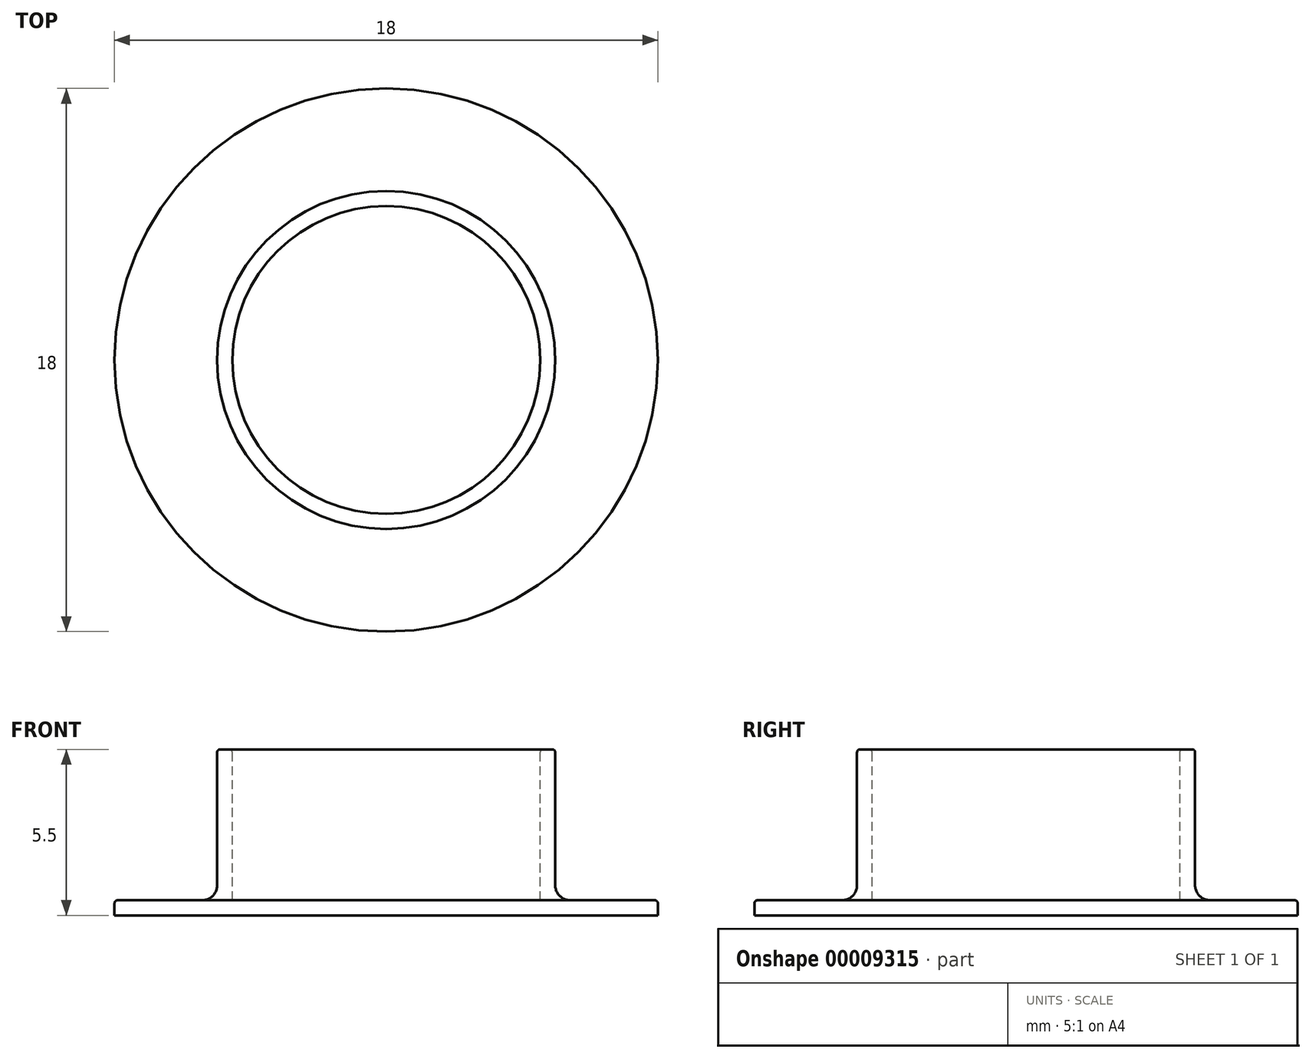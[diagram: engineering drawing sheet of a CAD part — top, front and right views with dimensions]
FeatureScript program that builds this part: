
annotation { "Feature Type Name" : "Feature", "Feature Type Description" : "" }
export const myFeature = defineFeature(function(context is Context, id is Id, definition is map)
    precondition{}
    {
        {
            var Q0;
            Q0=qCreatedBy(makeId("Right.planeOp"),FACE);
            var sketch = newSketch(context, id + "F0", { "sketchPlane" : qUnion([Q0])});
            skLineSegment(sketch, "E0", {"start": v(0, 0) * mm, "end": v(-9, 0) * mm});
            skLineSegment(sketch, "E1", {"start": v(-9, 0) * mm, "end": v(-9, 0.4) * mm});
            skLineSegment(sketch, "E2", {"start": v(-8.9, 0.5) * mm, "end": v(-6.1, 0.5) * mm});
            skLineSegment(sketch, "E3", {"start": v(0, 0.5) * mm, "end": v(0, 0) * mm});
            skLineSegment(sketch, "E4", {"start": v(-5.1, 0.5) * mm, "end": v(-5.1, 5.4) * mm});
            skLineSegment(sketch, "E5", {"start": v(-5.2, 5.5) * mm, "end": v(-5.5, 5.5) * mm});
            skLineSegment(sketch, "E6", {"start": v(-5.6, 5.4) * mm, "end": v(-5.6, 1) * mm});
            skPoint(sketch, "E7.newPointA", {"position": v(-5.6, 0.5) * mm});
            skPoint(sketch, "E7.newPointB", {"position": v(0, 0.5) * mm});
            skArc(sketch, "E7.filletArc", {"start": v(-6.1, 0.5) * mm, "mid": v(-5.75, 0.65) * mm, "end": v(-5.6, 1) * mm});
            skLineSegment(sketch, "E8", {"start": v(-5.1, 0.5) * mm, "end": v(0, 0.5) * mm});
            skPoint(sketch, "E9.visualSharp", {"position": v(-9, 0.5) * mm});
            skArc(sketch, "E9.filletArc", {"start": v(-8.9, 0.5) * mm, "mid": v(-8.97, 0.47) * mm, "end": v(-9, 0.4) * mm});
            skPoint(sketch, "E10.visualSharp", {"position": v(-5.6, 5.5) * mm});
            skArc(sketch, "E10.filletArc", {"start": v(-5.5, 5.5) * mm, "mid": v(-5.57, 5.47) * mm, "end": v(-5.6, 5.4) * mm});
            skPoint(sketch, "E11.visualSharp", {"position": v(-5.1, 5.5) * mm});
            skArc(sketch, "E11.filletArc", {"start": v(-5.1, 5.4) * mm, "mid": v(-5.13, 5.47) * mm, "end": v(-5.2, 5.5) * mm});
            skSolve(sketch);
        }
        {
            var Q0;
            Q0=makeQuery(id+"F0.imprint","IMPRINT",FACE,{"disambiguationData":[TD([[makeQuery(id+"F0.imprint","IMPRINT",EDGE,{"derivedFrom":sQuery(id+"F0.wireOp",EDGE,"E0")}),-1.0]])]});
            var sketch = newSketch(context, id + "F1", { "sketchPlane" : qUnion([Q0])});
            skLineSegment(sketch, "E12.0", {"start": v(-5.2, 5.5) * mm, "end": v(-5.5, 5.5) * mm, "construction": true});
            skLineSegment(sketch, "E13", {"start": v(0, 5.5) * mm, "end": v(0, 6) * mm});
            skLineSegment(sketch, "E14", {"start": v(0, 6) * mm, "end": v(-6, 6) * mm});
            skLineSegment(sketch, "E15", {"start": v(-6.1, 5.9) * mm, "end": v(-6.1, 2.1) * mm});
            skLineSegment(sketch, "E16", {"start": v(-5.6, 5.5) * mm, "end": v(0, 5.5) * mm});
            skLineSegment(sketch, "E17", {"start": v(-5.6, 5.5) * mm, "end": v(-5.6, 2) * mm});
            skLineSegment(sketch, "E18", {"start": v(-5.6, 2) * mm, "end": v(-6, 2) * mm});
            skPoint(sketch, "E19.visualSharp", {"position": v(-6.1, 6) * mm});
            skArc(sketch, "E19.filletArc", {"start": v(-6, 6) * mm, "mid": v(-6.07, 5.97) * mm, "end": v(-6.1, 5.9) * mm});
            skPoint(sketch, "E20.visualSharp", {"position": v(-6.1, 2) * mm});
            skArc(sketch, "E20.filletArc", {"start": v(-6.1, 2.1) * mm, "mid": v(-6.07, 2.03) * mm, "end": v(-6, 2) * mm});
            skSolve(sketch);
        }
        {
            var Q0;
            Q0=makeQuery(id+"F0.imprint","IMPRINT",FACE,{"disambiguationData":[TD([[makeQuery(id+"F0.imprint","IMPRINT",EDGE,{"derivedFrom":sQuery(id+"F0.wireOp",EDGE,"E0")}),-1.0]])]});
            var Q1;
            Q1=sQuery(id+"F0.wireOp",EDGE,"E3");
            revolve(context, id + "F2", {"entities" : qUnion([Q0]), "axis" : qUnion([Q1]), "revolveType" : RevolveType.FULL});
        }
        {
            var Q0;
            {var subQ7=sQuery(id+"F1.wireOp",EDGE,"E13");Q0=makeQuery(id+"F1.imprint","IMPRINT",FACE,{"disambiguationData":[TD([[makeQuery(id+"F1.imprint","IMPRINT",EDGE,{"derivedFrom":subQ7}),1.0]])]});}
            var Q1;
            Q1=sQuery(id+"F1.wireOp",EDGE,"E13");
            revolve(context, id + "F3", {"entities" : qUnion([Q0]), "axis" : qUnion([Q1]), "revolveType" : RevolveType.FULL});
        }
        {
            var Q0;
            Q0=makeQuery(id+"F3.opRevolve","SWEPT_BODY",BODY,{"disambiguationData":[OSD([sQuery(id+"F1.wireOp",EDGE,"E13"),sQuery(id+"F1.wireOp",EDGE,"E14"),sQuery(id+"F1.wireOp",EDGE,"E15"),sQuery(id+"F1.wireOp",EDGE,"E16"),sQuery(id+"F1.wireOp",EDGE,"E17"),sQuery(id+"F1.wireOp",EDGE,"E18"),sQuery(id+"F1.wireOp",EDGE,"E19.filletArc"),sQuery(id+"F1.wireOp",EDGE,"E20.filletArc")])]});
            deleteBodies(context, id + "F4", {"entities" : qUnion([Q0])});
        }
    });
